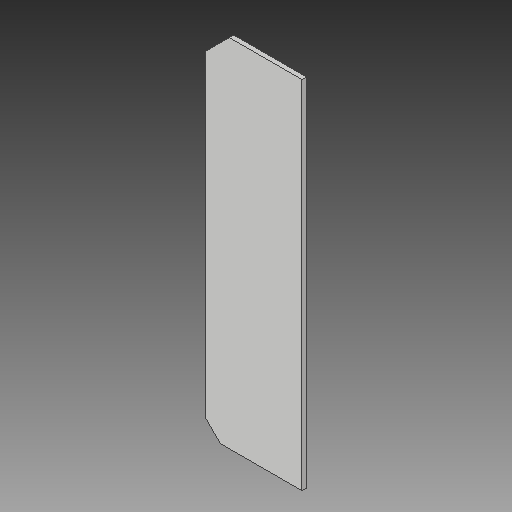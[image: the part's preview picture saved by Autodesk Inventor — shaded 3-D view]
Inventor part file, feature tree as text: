
AUTODESK INVENTOR PART (.ipt)
format: ipt  version: 2017 (Build 210142000, 142)  size: 98,304 bytes
history: native  units: in
note: dims shown in document units (in); Inventor stores cm internally (conversion verified against a paired STEP export)
features: chamfer x2, extrude x1, fillet x1, sketch x1
ambient origin geometry x8: Origin, YZ Plane, XZ Plane, XY Plane, X Axis, Y Axis, Z Axis, Center Point
bodies: Solid1 (feature_tree)
feature tree (5):
  extrude  "Extrusion1"  Depth=12.0in
  chamfer  "Chamfer1"  Distance=0.15in
  chamfer  "Chamfer2"  Distance=0.125in Angle=45.0deg
  fillet  "Fillet1"  Radius=0.125in
  sketch  "Sketch1"  dims[d0=3.25in d1=12.0in d2=0.15in d3=0.0in d4=0.5in d5=0.125in d6=45.0deg d7=0.8in d8=0.125in d9=45.0deg d10=0.125in]
